# Revit family: QF_VOLLRATH_FC-HCF-02120-ADFF
name_source: partatom
category: Generic Models
units: mm (PartAtom-declared; Revit-internal decimal feet)

## family parameters
Always vertical = No
Can host rebar = No
Cut with Voids When Loaded = No
OmniClass Number = 23.40.40.00
OmniClass Title = Food Service Equipment and Furnishings
Part Type = Normal
Room Calculation Point = No
Round Connector Dimension = Use Diameter
Shared = Yes
Work Plane-Based = Yes

## types (1)
- QF_VOLLRATH_FC-HCF-02120-ADFF
    Apparent Power = 1236 VA
    BTUH = 0.0 Btu/h
    Conn Conduit = Yes
    Conn Plug = NEMA 5-15P
    Cycle = 0 Hz
    Default Elevation = 48 "
    Elec Conn Connection Height = 0 "
    FL Amps = 10 A
    Foodservice Equipment Identifier = Yes
    IsLegacy_Config = 0
    IsLegacy_Custom = 0
    Manufacturer = Vollrath
    Max Overcurrent Protection = 0 A
    Min Ckt Ampacity = 0 A
    PartNo_Config = FC-6HCF-02208-ADFF
    PartNo_Custom = FC-6HCF-02208-ADFF
    Phase = 0
    Redraw_Config = 0
    Redraw_Custom = 0
    Refrigerant Type = R290
    Refrigerant Volume = 0.00 kip
    Volts = 120 V
    Watts = 0 W
    Weight in Pounds = 185

## geometry (parser evidence)
native form markers: Sweep x3
no freeform markers — native parametric forms only
